# Revit family: Robe_Hook-Bobrick-B-76717
name_source: partatom
category: Specialty Equipment
revit_build: Autodesk Revit 2014 (Build: 20130308_1515(x64)
units: mm (PartAtom-declared; Revit-internal decimal feet)

## types (2) — shared parameters
Assembly Code = C1030220
Default Elevation = 38"
Description = Surface Mounted Single Robe Hook
Height = 2"
Installation Type = Wall Mounted
Label = Clothing Hook
Length = 1 5/8"
Manufacturer = Bobrick
Price = Prices may vary. Please consult Manufacturer Representative for most up-to-date price list.
Product Documentation Link = http://products.bobrick.com
Product Page URL = http://products.bobrick.com
Revised Date = 02/07/2019
Type Comments = Available in bright polished stainless steel ot satin-finish stainless steel.
URL = http://www.bobrick.com
Width = 2"

## per-type parameters (varying)
| type | Finish | Material |
| B-76717 | Stainless Steel-Bobrick-Type 304-Satin | Stainless Steel-Bobrick-Type 304-Satin |
| B-7671 | Stainless Steel-Bobrick-Type 304-Bright Polished | Stainless Steel-Bobrick-Type 304-Bright Polished |

note: column(s) folded — value = type name in every type: Model

## geometry (parser evidence)
native form markers: Sweep x3
no freeform markers — native parametric forms only
